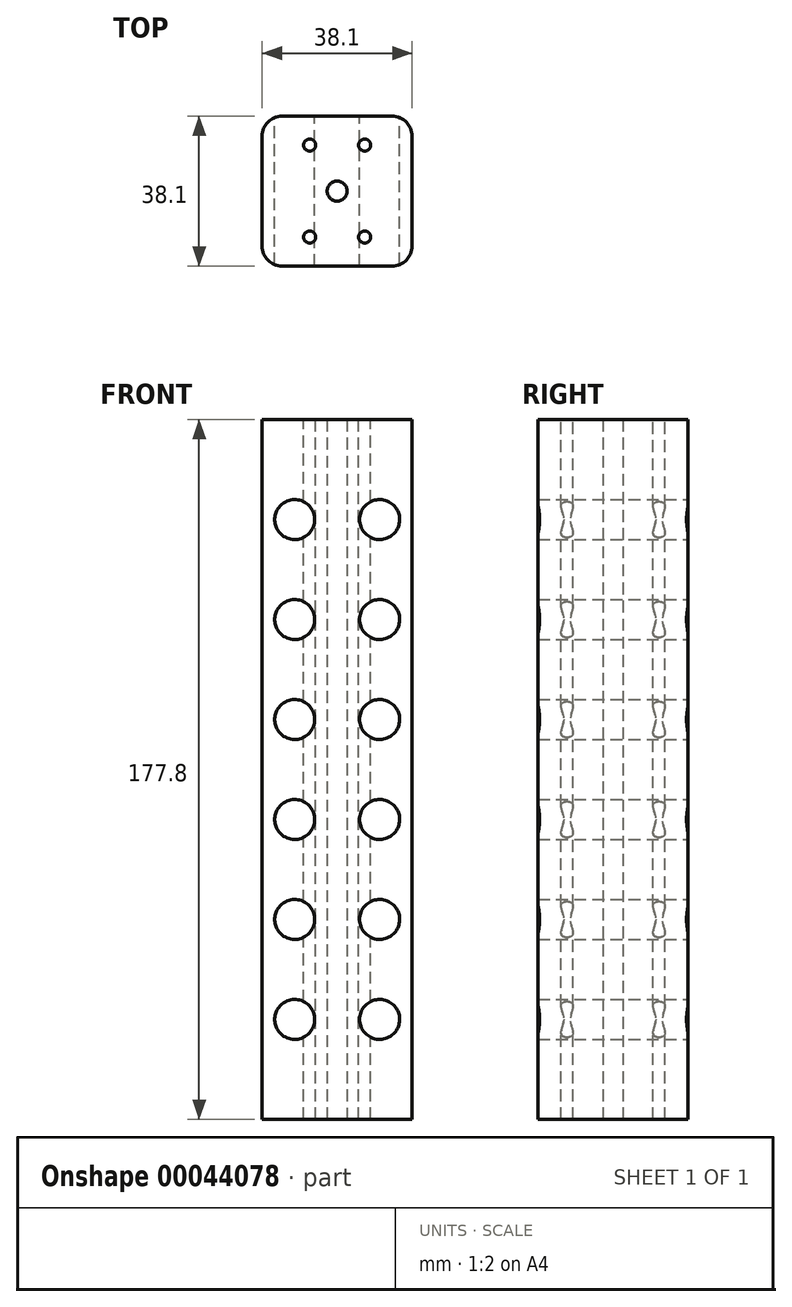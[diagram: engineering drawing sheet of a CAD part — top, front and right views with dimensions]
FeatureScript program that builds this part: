
annotation { "Feature Type Name" : "Feature", "Feature Type Description" : "" }
export const myFeature = defineFeature(function(context is Context, id is Id, definition is map)
    precondition{}
    {
        {
            var Q0;
            Q0=qCreatedBy(makeId("Top.planeOp"),FACE);
            var sketch = newSketch(context, id + "F0", { "sketchPlane" : qUnion([Q0])});
            skLineSegment(sketch, "E0.rect.bottom", {"start": v(19.05, 19.05) * mm, "end": v(-19.05, 19.05) * mm});
            skLineSegment(sketch, "E0.rect.top", {"start": v(19.05, -19.05) * mm, "end": v(-19.05, -19.05) * mm});
            skLineSegment(sketch, "E0.rect.left", {"start": v(19.05, 19.05) * mm, "end": v(19.05, -19.05) * mm});
            skLineSegment(sketch, "E0.rect.right", {"start": v(-19.05, 19.05) * mm, "end": v(-19.05, -19.05) * mm});
            skPoint(sketch, "E0.rect.middle", {"position": v(0, 0) * mm});
            skCircle(sketch, "E1", {"center": v(0, 0) * mm, "radius": 2.54 * mm});
            skSolve(sketch);
        }
        {
            var Q0;
            Q0=makeQuery(id+"F0.imprint","IMPRINT",FACE,{"disambiguationData":[TD([[makeQuery(id+"F0.imprint","IMPRINT",EDGE,{"derivedFrom":sQuery(id+"F0.wireOp",EDGE,"E0.rect.bottom")}),1.0]])]});
            extrude(context, id + "F1", {"entities" : qUnion([Q0]), "depth" : 177.8 * mm});
        }
        {
            var Q0;
            Q0=makeQuery(id+"F1.opExtrude","SWEPT_FACE",FACE,{"disambiguationData":[OSD([sQuery(id+"F0.wireOp",EDGE,"E0.rect.bottom")])]});
            var sketch = newSketch(context, id + "F2", { "sketchPlane" : qUnion([Q0])});
            skLineSegment(sketch, "E2.rect.bottom", {"start": v(-2.54, 0) * mm, "end": v(2.54, 0) * mm});
            skLineSegment(sketch, "E2.rect.top", {"start": v(-2.54, 177.8) * mm, "end": v(2.54, 177.8) * mm});
            skLineSegment(sketch, "E2.rect.left", {"start": v(-2.54, 0) * mm, "end": v(-2.54, 177.8) * mm});
            skLineSegment(sketch, "E2.rect.right", {"start": v(2.54, 0) * mm, "end": v(2.54, 177.8) * mm});
            skPoint(sketch, "E2.rect.middle", {"position": v(0, 88.9) * mm});
            skPoint(sketch, "E2.rect.middle.positionSnap0", {"position": v(19.05, 88.9) * mm});
            skPoint(sketch, "E2.rect.centerSnap0", {"position": v(19.05, 88.9) * mm});
            skLineSegment(sketch, "E3", {"start": v(19.05, 25.4) * mm, "end": v(-19.05, 25.4) * mm});
            skLineSegment(sketch, "E4", {"start": v(19.05, 50.8) * mm, "end": v(-19.05, 50.8) * mm});
            skLineSegment(sketch, "E5", {"start": v(19.05, 76.2) * mm, "end": v(-19.05, 76.2) * mm});
            skLineSegment(sketch, "E6", {"start": v(19.05, 101.6) * mm, "end": v(-19.05, 101.6) * mm});
            skLineSegment(sketch, "E7", {"start": v(19.05, 127) * mm, "end": v(-19.05, 127) * mm});
            skLineSegment(sketch, "E8", {"start": v(19.05, 152.4) * mm, "end": v(-19.05, 152.4) * mm});
            skLineSegment(sketch, "E9", {"start": v(19.05, 0) * mm, "end": v(2.54, 0) * mm, "construction": true});
            skLineSegment(sketch, "E10", {"start": v(10.8, 0) * mm, "end": v(10.8, 177.8) * mm, "construction": true});
            skLineSegment(sketch, "E11", {"start": v(-2.54, 0) * mm, "end": v(-19.05, 0) * mm, "construction": true});
            skLineSegment(sketch, "E12", {"start": v(-10.8, 0) * mm, "end": v(-10.8, 177.8) * mm, "construction": true});
            skCircle(sketch, "E13", {"center": v(-10.8, 25.4) * mm, "radius": 5.08 * mm});
            skCircle(sketch, "E14", {"center": v(-10.8, 50.8) * mm, "radius": 5.08 * mm});
            skCircle(sketch, "E15", {"center": v(-10.8, 76.2) * mm, "radius": 5.08 * mm});
            skCircle(sketch, "E16", {"center": v(-10.8, 101.6) * mm, "radius": 5.08 * mm});
            skCircle(sketch, "E17", {"center": v(-10.8, 127) * mm, "radius": 5.08 * mm});
            skCircle(sketch, "E18", {"center": v(-10.8, 152.4) * mm, "radius": 5.08 * mm});
            skCircle(sketch, "E19", {"center": v(10.8, 25.4) * mm, "radius": 5.08 * mm});
            skCircle(sketch, "E20", {"center": v(10.8, 50.8) * mm, "radius": 5.08 * mm});
            skCircle(sketch, "E21", {"center": v(10.8, 76.2) * mm, "radius": 5.08 * mm});
            skCircle(sketch, "E22", {"center": v(10.8, 101.6) * mm, "radius": 5.08 * mm});
            skCircle(sketch, "E23", {"center": v(10.8, 127) * mm, "radius": 5.08 * mm});
            skCircle(sketch, "E24", {"center": v(10.8, 152.4) * mm, "radius": 5.08 * mm});
            skSolve(sketch);
        }
        {
            var Q0;
            {var subQ0=sQuery(id+"F2.wireOp",EDGE,"E13");var subQ1=sQuery(id+"F2.wireOp",EDGE,"E3");var subQ3=makeQuery(id+"F2.imprint","INTERSECT",VERTEX,{"disambiguationData":[OD(0.0)],"derivedFrom":[subQ1,subQ0]});Q0=makeQuery(id+"F2.imprint","IMPRINT",FACE,{"disambiguationData":[TD([[makeQuery(id+"F2.imprint","IMPRINT",EDGE,{"disambiguationData":[TD([[subQ3,-1.0]])],"derivedFrom":subQ1}),1.0]])]});}
            var Q1;
            {var subQ0=sQuery(id+"F2.wireOp",EDGE,"E13");var subQ1=sQuery(id+"F2.wireOp",EDGE,"E3");var subQ3=makeQuery(id+"F2.imprint","INTERSECT",VERTEX,{"disambiguationData":[OD(0.0)],"derivedFrom":[subQ1,subQ0]});Q1=makeQuery(id+"F2.imprint","IMPRINT",FACE,{"disambiguationData":[TD([[makeQuery(id+"F2.imprint","IMPRINT",EDGE,{"disambiguationData":[TD([[subQ3,-1.0]])],"derivedFrom":subQ1}),-1.0]])]});}
            var Q2;
            {var subQ0=sQuery(id+"F2.wireOp",EDGE,"E19");var subQ1=sQuery(id+"F2.wireOp",EDGE,"E3");var subQ3=makeQuery(id+"F2.imprint","INTERSECT",VERTEX,{"disambiguationData":[OD(0.0)],"derivedFrom":[subQ1,subQ0]});Q2=makeQuery(id+"F2.imprint","IMPRINT",FACE,{"disambiguationData":[TD([[makeQuery(id+"F2.imprint","IMPRINT",EDGE,{"disambiguationData":[TD([[subQ3,-1.0]])],"derivedFrom":subQ1}),1.0]])]});}
            var Q3;
            {var subQ0=sQuery(id+"F2.wireOp",EDGE,"E20");var subQ1=sQuery(id+"F2.wireOp",EDGE,"E4");var subQ3=makeQuery(id+"F2.imprint","INTERSECT",VERTEX,{"disambiguationData":[OD(0.0)],"derivedFrom":[subQ1,subQ0]});Q3=makeQuery(id+"F2.imprint","IMPRINT",FACE,{"disambiguationData":[TD([[makeQuery(id+"F2.imprint","IMPRINT",EDGE,{"disambiguationData":[TD([[subQ3,-1.0]])],"derivedFrom":subQ1}),1.0]])]});}
            var Q4;
            {var subQ0=sQuery(id+"F2.wireOp",EDGE,"E20");var subQ1=sQuery(id+"F2.wireOp",EDGE,"E4");var subQ3=makeQuery(id+"F2.imprint","INTERSECT",VERTEX,{"disambiguationData":[OD(0.0)],"derivedFrom":[subQ1,subQ0]});Q4=makeQuery(id+"F2.imprint","IMPRINT",FACE,{"disambiguationData":[TD([[makeQuery(id+"F2.imprint","IMPRINT",EDGE,{"disambiguationData":[TD([[subQ3,-1.0]])],"derivedFrom":subQ1}),-1.0]])]});}
            var Q5;
            {var subQ0=sQuery(id+"F2.wireOp",EDGE,"E14");var subQ1=sQuery(id+"F2.wireOp",EDGE,"E4");var subQ3=makeQuery(id+"F2.imprint","INTERSECT",VERTEX,{"disambiguationData":[OD(0.0)],"derivedFrom":[subQ1,subQ0]});Q5=makeQuery(id+"F2.imprint","IMPRINT",FACE,{"disambiguationData":[TD([[makeQuery(id+"F2.imprint","IMPRINT",EDGE,{"disambiguationData":[TD([[subQ3,-1.0]])],"derivedFrom":subQ1}),-1.0]])]});}
            var Q6;
            {var subQ0=sQuery(id+"F2.wireOp",EDGE,"E14");var subQ1=sQuery(id+"F2.wireOp",EDGE,"E4");var subQ3=makeQuery(id+"F2.imprint","INTERSECT",VERTEX,{"disambiguationData":[OD(0.0)],"derivedFrom":[subQ1,subQ0]});Q6=makeQuery(id+"F2.imprint","IMPRINT",FACE,{"disambiguationData":[TD([[makeQuery(id+"F2.imprint","IMPRINT",EDGE,{"disambiguationData":[TD([[subQ3,-1.0]])],"derivedFrom":subQ1}),1.0]])]});}
            var Q7;
            {var subQ0=sQuery(id+"F2.wireOp",EDGE,"E15");var subQ1=sQuery(id+"F2.wireOp",EDGE,"E5");var subQ3=makeQuery(id+"F2.imprint","INTERSECT",VERTEX,{"disambiguationData":[OD(0.0)],"derivedFrom":[subQ1,subQ0]});Q7=makeQuery(id+"F2.imprint","IMPRINT",FACE,{"disambiguationData":[TD([[makeQuery(id+"F2.imprint","IMPRINT",EDGE,{"disambiguationData":[TD([[subQ3,-1.0]])],"derivedFrom":subQ1}),-1.0]])]});}
            var Q8;
            {var subQ0=sQuery(id+"F2.wireOp",EDGE,"E21");var subQ1=sQuery(id+"F2.wireOp",EDGE,"E5");var subQ3=makeQuery(id+"F2.imprint","INTERSECT",VERTEX,{"disambiguationData":[OD(0.0)],"derivedFrom":[subQ1,subQ0]});Q8=makeQuery(id+"F2.imprint","IMPRINT",FACE,{"disambiguationData":[TD([[makeQuery(id+"F2.imprint","IMPRINT",EDGE,{"disambiguationData":[TD([[subQ3,-1.0]])],"derivedFrom":subQ1}),1.0]])]});}
            var Q9;
            {var subQ0=sQuery(id+"F2.wireOp",EDGE,"E21");var subQ1=sQuery(id+"F2.wireOp",EDGE,"E5");var subQ3=makeQuery(id+"F2.imprint","INTERSECT",VERTEX,{"disambiguationData":[OD(0.0)],"derivedFrom":[subQ1,subQ0]});Q9=makeQuery(id+"F2.imprint","IMPRINT",FACE,{"disambiguationData":[TD([[makeQuery(id+"F2.imprint","IMPRINT",EDGE,{"disambiguationData":[TD([[subQ3,-1.0]])],"derivedFrom":subQ1}),-1.0]])]});}
            var Q10;
            {var subQ0=sQuery(id+"F2.wireOp",EDGE,"E22");var subQ1=sQuery(id+"F2.wireOp",EDGE,"E6");var subQ3=makeQuery(id+"F2.imprint","INTERSECT",VERTEX,{"disambiguationData":[OD(0.0)],"derivedFrom":[subQ1,subQ0]});Q10=makeQuery(id+"F2.imprint","IMPRINT",FACE,{"disambiguationData":[TD([[makeQuery(id+"F2.imprint","IMPRINT",EDGE,{"disambiguationData":[TD([[subQ3,-1.0]])],"derivedFrom":subQ1}),1.0]])]});}
            var Q11;
            {var subQ0=sQuery(id+"F2.wireOp",EDGE,"E22");var subQ1=sQuery(id+"F2.wireOp",EDGE,"E6");var subQ3=makeQuery(id+"F2.imprint","INTERSECT",VERTEX,{"disambiguationData":[OD(0.0)],"derivedFrom":[subQ1,subQ0]});Q11=makeQuery(id+"F2.imprint","IMPRINT",FACE,{"disambiguationData":[TD([[makeQuery(id+"F2.imprint","IMPRINT",EDGE,{"disambiguationData":[TD([[subQ3,-1.0]])],"derivedFrom":subQ1}),-1.0]])]});}
            var Q12;
            {var subQ0=sQuery(id+"F2.wireOp",EDGE,"E16");var subQ1=sQuery(id+"F2.wireOp",EDGE,"E6");var subQ3=makeQuery(id+"F2.imprint","INTERSECT",VERTEX,{"disambiguationData":[OD(0.0)],"derivedFrom":[subQ1,subQ0]});Q12=makeQuery(id+"F2.imprint","IMPRINT",FACE,{"disambiguationData":[TD([[makeQuery(id+"F2.imprint","IMPRINT",EDGE,{"disambiguationData":[TD([[subQ3,-1.0]])],"derivedFrom":subQ1}),1.0]])]});}
            var Q13;
            {var subQ0=sQuery(id+"F2.wireOp",EDGE,"E16");var subQ1=sQuery(id+"F2.wireOp",EDGE,"E6");var subQ3=makeQuery(id+"F2.imprint","INTERSECT",VERTEX,{"disambiguationData":[OD(0.0)],"derivedFrom":[subQ1,subQ0]});Q13=makeQuery(id+"F2.imprint","IMPRINT",FACE,{"disambiguationData":[TD([[makeQuery(id+"F2.imprint","IMPRINT",EDGE,{"disambiguationData":[TD([[subQ3,-1.0]])],"derivedFrom":subQ1}),-1.0]])]});}
            var Q14;
            {var subQ0=sQuery(id+"F2.wireOp",EDGE,"E19");var subQ1=sQuery(id+"F2.wireOp",EDGE,"E3");var subQ3=makeQuery(id+"F2.imprint","INTERSECT",VERTEX,{"disambiguationData":[OD(0.0)],"derivedFrom":[subQ1,subQ0]});Q14=makeQuery(id+"F2.imprint","IMPRINT",FACE,{"disambiguationData":[TD([[makeQuery(id+"F2.imprint","IMPRINT",EDGE,{"disambiguationData":[TD([[subQ3,-1.0]])],"derivedFrom":subQ1}),-1.0]])]});}
            var Q15;
            {var subQ0=sQuery(id+"F2.wireOp",EDGE,"E23");var subQ1=sQuery(id+"F2.wireOp",EDGE,"E7");var subQ3=makeQuery(id+"F2.imprint","INTERSECT",VERTEX,{"disambiguationData":[OD(0.0)],"derivedFrom":[subQ1,subQ0]});Q15=makeQuery(id+"F2.imprint","IMPRINT",FACE,{"disambiguationData":[TD([[makeQuery(id+"F2.imprint","IMPRINT",EDGE,{"disambiguationData":[TD([[subQ3,-1.0]])],"derivedFrom":subQ1}),1.0]])]});}
            var Q16;
            {var subQ0=sQuery(id+"F2.wireOp",EDGE,"E23");var subQ1=sQuery(id+"F2.wireOp",EDGE,"E7");var subQ3=makeQuery(id+"F2.imprint","INTERSECT",VERTEX,{"disambiguationData":[OD(0.0)],"derivedFrom":[subQ1,subQ0]});Q16=makeQuery(id+"F2.imprint","IMPRINT",FACE,{"disambiguationData":[TD([[makeQuery(id+"F2.imprint","IMPRINT",EDGE,{"disambiguationData":[TD([[subQ3,-1.0]])],"derivedFrom":subQ1}),-1.0]])]});}
            var Q17;
            {var subQ0=sQuery(id+"F2.wireOp",EDGE,"E17");var subQ1=sQuery(id+"F2.wireOp",EDGE,"E7");var subQ3=makeQuery(id+"F2.imprint","INTERSECT",VERTEX,{"disambiguationData":[OD(0.0)],"derivedFrom":[subQ1,subQ0]});Q17=makeQuery(id+"F2.imprint","IMPRINT",FACE,{"disambiguationData":[TD([[makeQuery(id+"F2.imprint","IMPRINT",EDGE,{"disambiguationData":[TD([[subQ3,-1.0]])],"derivedFrom":subQ1}),1.0]])]});}
            var Q18;
            {var subQ0=sQuery(id+"F2.wireOp",EDGE,"E17");var subQ1=sQuery(id+"F2.wireOp",EDGE,"E7");var subQ3=makeQuery(id+"F2.imprint","INTERSECT",VERTEX,{"disambiguationData":[OD(0.0)],"derivedFrom":[subQ1,subQ0]});Q18=makeQuery(id+"F2.imprint","IMPRINT",FACE,{"disambiguationData":[TD([[makeQuery(id+"F2.imprint","IMPRINT",EDGE,{"disambiguationData":[TD([[subQ3,-1.0]])],"derivedFrom":subQ1}),-1.0]])]});}
            var Q19;
            {var subQ0=sQuery(id+"F2.wireOp",EDGE,"E18");var subQ1=sQuery(id+"F2.wireOp",EDGE,"E8");var subQ3=makeQuery(id+"F2.imprint","INTERSECT",VERTEX,{"disambiguationData":[OD(0.0)],"derivedFrom":[subQ1,subQ0]});Q19=makeQuery(id+"F2.imprint","IMPRINT",FACE,{"disambiguationData":[TD([[makeQuery(id+"F2.imprint","IMPRINT",EDGE,{"disambiguationData":[TD([[subQ3,-1.0]])],"derivedFrom":subQ1}),1.0]])]});}
            var Q20;
            {var subQ0=sQuery(id+"F2.wireOp",EDGE,"E18");var subQ1=sQuery(id+"F2.wireOp",EDGE,"E8");var subQ3=makeQuery(id+"F2.imprint","INTERSECT",VERTEX,{"disambiguationData":[OD(0.0)],"derivedFrom":[subQ1,subQ0]});Q20=makeQuery(id+"F2.imprint","IMPRINT",FACE,{"disambiguationData":[TD([[makeQuery(id+"F2.imprint","IMPRINT",EDGE,{"disambiguationData":[TD([[subQ3,-1.0]])],"derivedFrom":subQ1}),-1.0]])]});}
            var Q21;
            {var subQ0=sQuery(id+"F2.wireOp",EDGE,"E24");var subQ1=sQuery(id+"F2.wireOp",EDGE,"E8");var subQ3=makeQuery(id+"F2.imprint","INTERSECT",VERTEX,{"disambiguationData":[OD(0.0)],"derivedFrom":[subQ1,subQ0]});Q21=makeQuery(id+"F2.imprint","IMPRINT",FACE,{"disambiguationData":[TD([[makeQuery(id+"F2.imprint","IMPRINT",EDGE,{"disambiguationData":[TD([[subQ3,-1.0]])],"derivedFrom":subQ1}),1.0]])]});}
            var Q22;
            {var subQ0=sQuery(id+"F2.wireOp",EDGE,"E24");var subQ1=sQuery(id+"F2.wireOp",EDGE,"E8");var subQ3=makeQuery(id+"F2.imprint","INTERSECT",VERTEX,{"disambiguationData":[OD(0.0)],"derivedFrom":[subQ1,subQ0]});Q22=makeQuery(id+"F2.imprint","IMPRINT",FACE,{"disambiguationData":[TD([[makeQuery(id+"F2.imprint","IMPRINT",EDGE,{"disambiguationData":[TD([[subQ3,-1.0]])],"derivedFrom":subQ1}),-1.0]])]});}
            var Q23;
            {var subQ0=sQuery(id+"F2.wireOp",EDGE,"E15");var subQ1=sQuery(id+"F2.wireOp",EDGE,"E5");var subQ3=makeQuery(id+"F2.imprint","INTERSECT",VERTEX,{"disambiguationData":[OD(0.0)],"derivedFrom":[subQ1,subQ0]});Q23=makeQuery(id+"F2.imprint","IMPRINT",FACE,{"disambiguationData":[TD([[makeQuery(id+"F2.imprint","IMPRINT",EDGE,{"disambiguationData":[TD([[subQ3,-1.0]])],"derivedFrom":subQ1}),1.0]])]});}
            extrude(context, id + "F3", {"entities" : qUnion([Q0, Q1, Q2, Q3, Q4, Q5, Q6, Q7, Q8, Q9, Q10, Q11, Q12, Q13, Q14, Q15, Q16, Q17, Q18, Q19, Q20, Q21, Q22, Q23]), "operationType" : NewBodyOperationType.REMOVE, "oppositeDirection" : true, "depth" : 50.8 * mm});
        }
        {
            var Q0;
            Q0=makeQuery(id+"F1.opExtrude","SWEPT_EDGE",EDGE,{"disambiguationData":[OSD([sQuery(id+"F0.wireOp",EDGE,"E0.rect.bottom"),sQuery(id+"F0.wireOp",EDGE,"E0.rect.left")])]});
            var Q1;
            Q1=makeQuery(id+"F1.opExtrude","SWEPT_EDGE",EDGE,{"disambiguationData":[OSD([sQuery(id+"F0.wireOp",EDGE,"E0.rect.top"),sQuery(id+"F0.wireOp",EDGE,"E0.rect.left")])]});
            var Q2;
            Q2=makeQuery(id+"F1.opExtrude","SWEPT_EDGE",EDGE,{"disambiguationData":[OSD([sQuery(id+"F0.wireOp",EDGE,"E0.rect.top"),sQuery(id+"F0.wireOp",EDGE,"E0.rect.right")])]});
            var Q3;
            Q3=makeQuery(id+"F1.opExtrude","SWEPT_EDGE",EDGE,{"disambiguationData":[OSD([sQuery(id+"F0.wireOp",EDGE,"E0.rect.bottom"),sQuery(id+"F0.wireOp",EDGE,"E0.rect.right")])]});
            fillet(context, id + "F4", {"entities" : qUnion([Q0, Q1, Q2, Q3]), "radius" : 5.08 * mm, "tangentPropagation" : true, "allowEdgeOverflow" : false});
        }
        {
            var Q0;
            Q0=makeQuery(id+"F1.opExtrude","CAP_FACE",FACE,{"disambiguationData":[OSD([sQuery(id+"F0.wireOp",EDGE,"E0.rect.bottom"),sQuery(id+"F0.wireOp",EDGE,"E0.rect.top"),sQuery(id+"F0.wireOp",EDGE,"E0.rect.left"),sQuery(id+"F0.wireOp",EDGE,"E0.rect.right"),sQuery(id+"F0.wireOp",EDGE,"E1")])],"isStart":false});
            var sketch = newSketch(context, id + "F5", { "sketchPlane" : qUnion([Q0])});
            skLineSegment(sketch, "E25", {"start": v(-13.97, 19.05) * mm, "end": v(13.97, 19.05) * mm});
            skLineSegment(sketch, "E26", {"start": v(-13.97, -19.05) * mm, "end": v(13.97, -19.05) * mm});
            skLineSegment(sketch, "E27", {"start": v(-13.97, -19.05) * mm, "end": v(-13.97, 19.05) * mm});
            skLineSegment(sketch, "E28", {"start": v(13.97, -19.05) * mm, "end": v(13.97, 19.05) * mm});
            skLineSegment(sketch, "E29", {"start": v(-13.97, 0) * mm, "end": v(13.97, 0) * mm});
            skLineSegment(sketch, "E30", {"start": v(0, 19.05) * mm, "end": v(0, -19.05) * mm});
            skLineSegment(sketch, "E31", {"start": v(0, 0) * mm, "end": v(0, 19.05) * mm});
            skLineSegment(sketch, "E32", {"start": v(0, 0) * mm, "end": v(0, -19.05) * mm});
            skPoint(sketch, "E33.centerSnap0", {"position": v(0, 9.53) * mm});
            skLineSegment(sketch, "E34", {"start": v(-13.97, 0) * mm, "end": v(0, 0) * mm});
            skLineSegment(sketch, "E35", {"start": v(0, 0) * mm, "end": v(13.97, 0) * mm});
            skCircle(sketch, "E36", {"center": v(-6.98, 11.68) * mm, "radius": 1.52 * mm});
            skPoint(sketch, "E36.centerSnap0", {"position": v(-6.99, 0) * mm});
            skCircle(sketch, "E37", {"center": v(-6.99, -11.68) * mm, "radius": 1.52 * mm});
            skCircle(sketch, "E38", {"center": v(6.98, 11.68) * mm, "radius": 1.52 * mm});
            skPoint(sketch, "E38.centerSnap0", {"position": v(6.98, 0) * mm});
            skCircle(sketch, "E39", {"center": v(6.98, -11.68) * mm, "radius": 1.52 * mm});
            skSolve(sketch);
        }
        {
            var Q0;
            Q0=makeQuery(id+"F5.imprint","IMPRINT",FACE,{"disambiguationData":[TD([[makeQuery(id+"F5.imprint","IMPRINT",EDGE,{"derivedFrom":sQuery(id+"F5.wireOp",EDGE,"E37")}),1.0]])]});
            var Q1;
            Q1=makeQuery(id+"F5.imprint","IMPRINT",FACE,{"disambiguationData":[TD([[makeQuery(id+"F5.imprint","IMPRINT",EDGE,{"derivedFrom":sQuery(id+"F5.wireOp",EDGE,"E39")}),1.0]])]});
            var Q2;
            Q2=makeQuery(id+"F5.imprint","IMPRINT",FACE,{"disambiguationData":[TD([[makeQuery(id+"F5.imprint","IMPRINT",EDGE,{"derivedFrom":sQuery(id+"F5.wireOp",EDGE,"E38")}),1.0]])]});
            var Q3;
            Q3=makeQuery(id+"F5.imprint","IMPRINT",FACE,{"disambiguationData":[TD([[makeQuery(id+"F5.imprint","IMPRINT",EDGE,{"derivedFrom":sQuery(id+"F5.wireOp",EDGE,"E36")}),1.0]])]});
            extrude(context, id + "F6", {"entities" : qUnion([Q0, Q1, Q2, Q3]), "operationType" : NewBodyOperationType.REMOVE, "oppositeDirection" : true, "depth" : 177.8 * mm});
        }
    });
